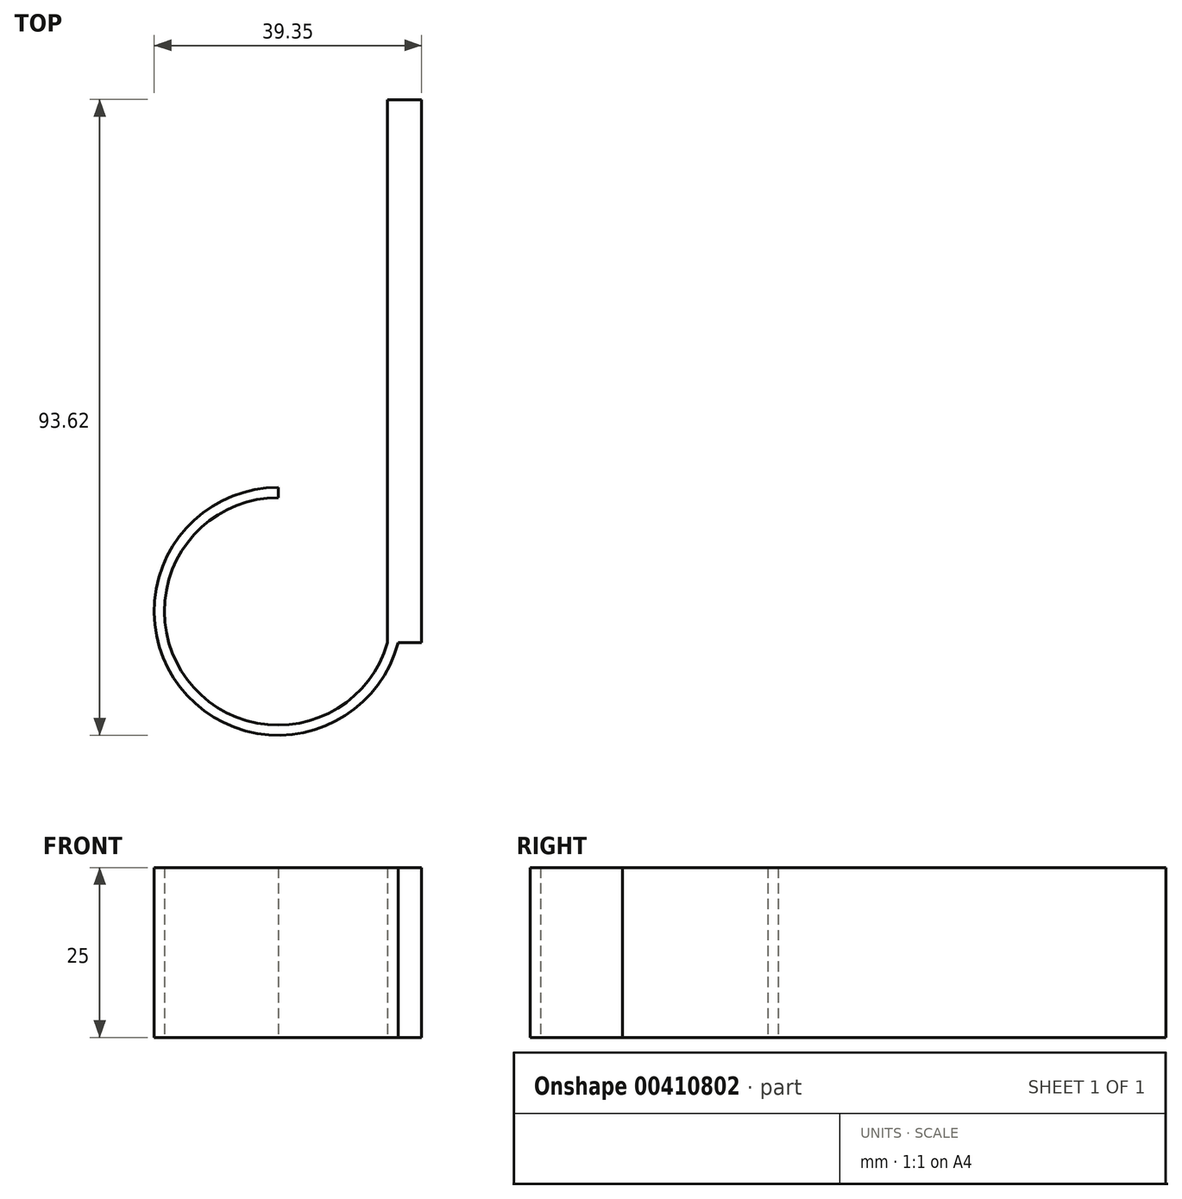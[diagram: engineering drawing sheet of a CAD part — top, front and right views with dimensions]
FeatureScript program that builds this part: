
annotation { "Feature Type Name" : "Feature", "Feature Type Description" : "" }
export const myFeature = defineFeature(function(context is Context, id is Id, definition is map)
    precondition{}
    {
        {
            var Q0;
            Q0=qCreatedBy(makeId("Top.planeOp"),FACE);
            var sketch = newSketch(context, id + "F0", { "sketchPlane" : qUnion([Q0])});
            skArc(sketch, "E0", {"start": v(0, 16.75) * mm, "mid": v(-13.38, -10.07) * mm, "end": v(16.1, -4.63) * mm});
            skPoint(sketch, "E1.end.orphan", {"position": v(0, 22.14) * mm});
            skLineSegment(sketch, "E2", {"start": v(16.1, -4.63) * mm, "end": v(21.1, -4.63) * mm});
            skLineSegment(sketch, "E3", {"start": v(21.1, -4.63) * mm, "end": v(21.1, 75.37) * mm});
            skLineSegment(sketch, "E4", {"start": v(21.1, 75.37) * mm, "end": v(16.1, 75.37) * mm});
            skLineSegment(sketch, "E5", {"start": v(16.1, 75.37) * mm, "end": v(16.1, -4.63) * mm});
            skArc(sketch, "E6", {"start": v(0, 18.25) * mm, "mid": v(-14.45, -11.15) * mm, "end": v(17.65, -4.63) * mm});
            skLineSegment(sketch, "E7", {"start": v(0, 18.25) * mm, "end": v(0, 16.75) * mm});
            skSolve(sketch);
        }
        {
            var Q0;
            Q0 = qSketchRegion(id + "F0", true);
            extrude(context, id + "F1", {"entities" : qUnion([Q0]), "depth" : 25 * mm});
        }
    });
